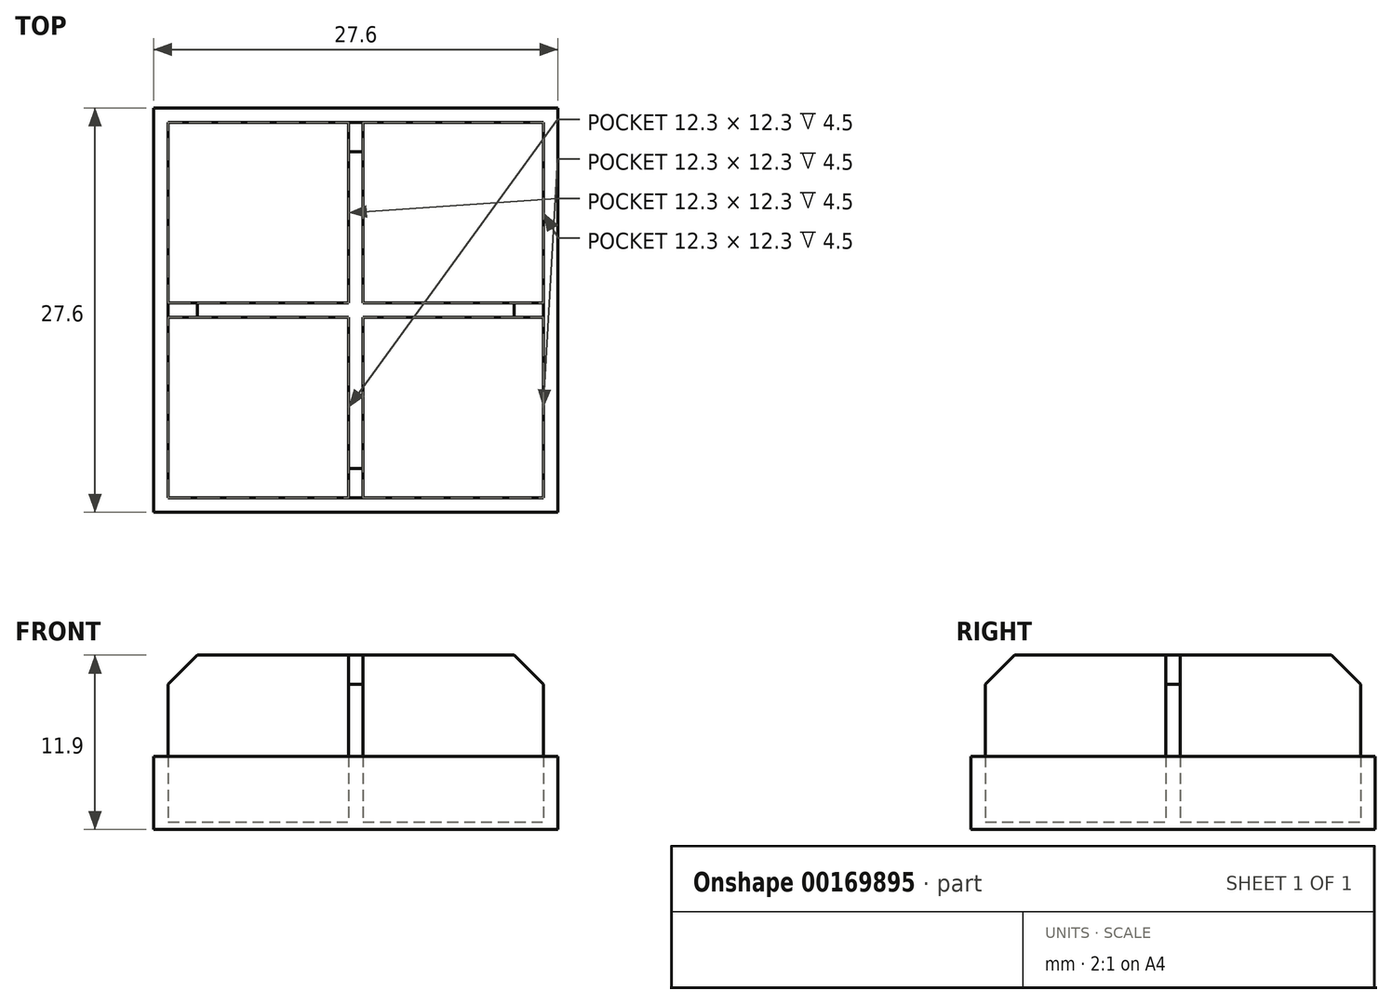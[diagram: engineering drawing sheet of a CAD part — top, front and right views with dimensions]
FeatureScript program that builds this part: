
annotation { "Feature Type Name" : "Feature", "Feature Type Description" : "" }
export const myFeature = defineFeature(function(context is Context, id is Id, definition is map)
    precondition{}
    {
        {
            var Q0;
            Q0=qCreatedBy(makeId("Top.planeOp"),FACE);
            var sketch = newSketch(context, id + "F0", { "sketchPlane" : qUnion([Q0])});
            skLineSegment(sketch, "E0.bottom", {"start": v(-13.8, -13.5) * mm, "end": v(13.8, -13.5) * mm});
            skLineSegment(sketch, "E0.top", {"start": v(-13.8, 14.1) * mm, "end": v(13.8, 14.1) * mm});
            skLineSegment(sketch, "E0.left", {"start": v(-13.8, -13.5) * mm, "end": v(-13.8, 14.1) * mm});
            skLineSegment(sketch, "E0.right", {"start": v(13.8, -13.5) * mm, "end": v(13.8, 14.1) * mm});
            skPoint(sketch, "E1", {"position": v(0, -13.5) * mm});
            skLineSegment(sketch, "E2.0", {"start": v(-12.8, 13.1) * mm, "end": v(12.8, 13.1) * mm});
            skLineSegment(sketch, "E2.1", {"start": v(-12.8, -12.5) * mm, "end": v(-12.8, 13.1) * mm});
            skLineSegment(sketch, "E2.2", {"start": v(-12.8, -12.5) * mm, "end": v(12.8, -12.5) * mm});
            skLineSegment(sketch, "E2.3", {"start": v(12.8, -12.5) * mm, "end": v(12.8, 13.1) * mm});
            skLineSegment(sketch, "E3.0", {"start": v(-12.8, -0.2) * mm, "end": v(-0.5, -0.2) * mm});
            skLineSegment(sketch, "E4.0", {"start": v(-12.8, 0.8) * mm, "end": v(-0.5, 0.8) * mm});
            skLineSegment(sketch, "E5.0", {"start": v(-0.5, -12.5) * mm, "end": v(-0.5, -0.2) * mm});
            skLineSegment(sketch, "E6.0", {"start": v(0.5, -12.5) * mm, "end": v(0.5, -0.2) * mm});
            skLineSegment(sketch, "E7.trimOffspring", {"start": v(-0.5, 0.8) * mm, "end": v(-0.5, 13.1) * mm});
            skLineSegment(sketch, "E8.trimOffspring", {"start": v(0.5, 0.8) * mm, "end": v(12.8, 0.8) * mm});
            skLineSegment(sketch, "E9.trimOffspring", {"start": v(0.5, 0.8) * mm, "end": v(0.5, 13.1) * mm});
            skLineSegment(sketch, "E10.trimOffspring", {"start": v(0.5, -0.2) * mm, "end": v(12.8, -0.2) * mm});
            skSolve(sketch);
        }
        {
            var Q0;
            {var subQ3=sQuery(id+"F0.wireOp",EDGE,"E3.0");Q0=makeQuery(id+"F0.imprint","IMPRINT",FACE,{"disambiguationData":[TD([[makeQuery(id+"F0.imprint","IMPRINT",EDGE,{"derivedFrom":subQ3}),1.0]])]});}
            extrude(context, id + "F1", {"entities" : qUnion([Q0]), "depth" : 11.9 * mm});
        }
        {
            var Q0;
            Q0=makeQuery(id+"F0.imprint","IMPRINT",FACE,{"disambiguationData":[TD([[makeQuery(id+"F0.imprint","IMPRINT",EDGE,{"derivedFrom":sQuery(id+"F0.wireOp",EDGE,"E0.bottom")}),1.0]])]});
            extrude(context, id + "F2", {"entities" : qUnion([Q0]), "operationType" : NewBodyOperationType.ADD, "depth" : 5 * mm});
        }
        {
            var Q0;
            Q0=qCreatedBy(makeId("Top.planeOp"),FACE);
            var sketch = newSketch(context, id + "F3", { "sketchPlane" : qUnion([Q0])});
            skLineSegment(sketch, "E11.bottom", {"start": v(-13.5, -13.5) * mm, "end": v(13.5, -13.5) * mm});
            skLineSegment(sketch, "E11.top", {"start": v(-13.5, 13.5) * mm, "end": v(13.5, 13.5) * mm});
            skLineSegment(sketch, "E11.left", {"start": v(-13.5, -13.5) * mm, "end": v(-13.5, 13.5) * mm});
            skLineSegment(sketch, "E11.right", {"start": v(13.5, -13.5) * mm, "end": v(13.5, 13.5) * mm});
            skSolve(sketch);
        }
        {
            var Q0;
            Q0=makeQuery(id+"F3.imprint","IMPRINT",FACE,{"disambiguationData":[TD([[makeQuery(id+"F3.imprint","IMPRINT",EDGE,{"derivedFrom":sQuery(id+"F3.wireOp",EDGE,"E11.bottom")}),1.0]])]});
            extrude(context, id + "F4", {"entities" : qUnion([Q0]), "operationType" : NewBodyOperationType.ADD, "depth" : 0.5 * mm});
        }
        {
            var Q0;
            Q0=makeQuery(id+"F1.opExtrude","CAP_EDGE",EDGE,{"disambiguationData":[OSD([sQuery(id+"F0.wireOp",EDGE,"E2.0")])],"isStart":false});
            var Q1;
            Q1=makeQuery(id+"F1.opExtrude","CAP_EDGE",EDGE,{"disambiguationData":[OSD([sQuery(id+"F0.wireOp",EDGE,"E2.1")])],"isStart":false});
            var Q2;
            Q2=makeQuery(id+"F1.opExtrude","CAP_EDGE",EDGE,{"disambiguationData":[OSD([sQuery(id+"F0.wireOp",EDGE,"E2.2")])],"isStart":false});
            var Q3;
            Q3=makeQuery(id+"F1.opExtrude","CAP_EDGE",EDGE,{"disambiguationData":[OSD([sQuery(id+"F0.wireOp",EDGE,"E2.3")])],"isStart":false});
            chamfer(context, id + "F5", {"entities" : qUnion([Q0, Q1, Q2, Q3]), "width" : 2 * mm, "tangentPropagation" : true});
        }
    });
